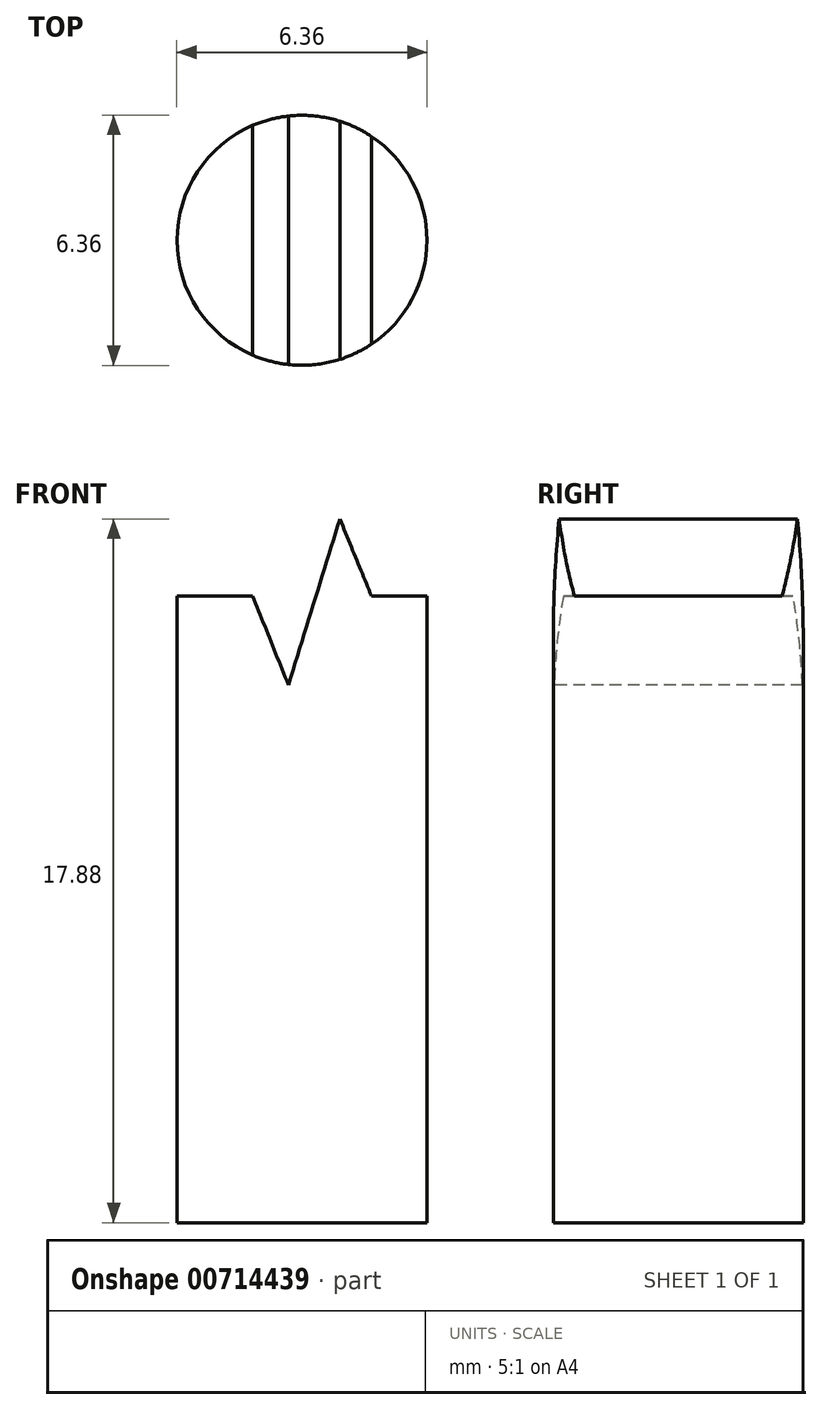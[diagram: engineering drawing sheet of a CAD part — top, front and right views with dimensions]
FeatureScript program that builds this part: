
annotation { "Feature Type Name" : "Feature", "Feature Type Description" : "" }
export const myFeature = defineFeature(function(context is Context, id is Id, definition is map)
    precondition{}
    {
        {
            var Q0;
            Q0=qCreatedBy(makeId("Top.planeOp"),FACE);
            var sketch = newSketch(context, id + "F0", { "sketchPlane" : qUnion([Q0])});
            skCircle(sketch, "E0", {"center": v(0, 0) * mm, "radius": 3.17 * mm});
            skSolve(sketch);
        }
        {
            var Q0;
            Q0=qSketchRegion(id+"F0",true);
            extrude(context, id + "F1", {"entities" : qUnion([Q0]), "oppositeDirection" : true, "depth" : 19.05 * mm});
        }
        {
            var Q0;
            Q0=qCreatedBy(makeId("Front.planeOp"),FACE);
            var sketch = newSketch(context, id + "F2", { "sketchPlane" : qUnion([Q0])});
            skLineSegment(sketch, "E1", {"start": v(-3.58, 0.1) * mm, "end": v(3.41, 0.1) * mm});
            skLineSegment(sketch, "E2", {"start": v(-3.58, -3.13) * mm, "end": v(-3.58, 0.1) * mm});
            skLineSegment(sketch, "E3", {"start": v(-3.58, -3.13) * mm, "end": v(-1.25, -3.13) * mm});
            skLineSegment(sketch, "E4", {"start": v(-0.34, -5.4) * mm, "end": v(-1.25, -3.13) * mm});
            skLineSegment(sketch, "E5", {"start": v(-0.34, -5.4) * mm, "end": v(0.96, -1.17) * mm});
            skLineSegment(sketch, "E6", {"start": v(0.96, -1.17) * mm, "end": v(1.77, -3.13) * mm});
            skLineSegment(sketch, "E7", {"start": v(1.77, -3.13) * mm, "end": v(3.5, -3.13) * mm});
            skLineSegment(sketch, "E8", {"start": v(3.41, 0.1) * mm, "end": v(3.5, -3.13) * mm});
            skSolve(sketch);
        }
        {
            var Q0;
            Q0=makeQuery(id+"F2.imprint","IMPRINT",FACE,{"disambiguationData":[TD([[makeQuery(id+"F2.imprint","IMPRINT",EDGE,{"derivedFrom":sQuery(id+"F2.wireOp",EDGE,"E1")}),-1.0]])]});
            extrude(context, id + "F3", {"entities" : qUnion([Q0]), "operationType" : NewBodyOperationType.REMOVE, "endBound" : BoundingType.SYMMETRIC, "oppositeDirection" : true, "depth" : 25.4 * mm});
        }
    });
